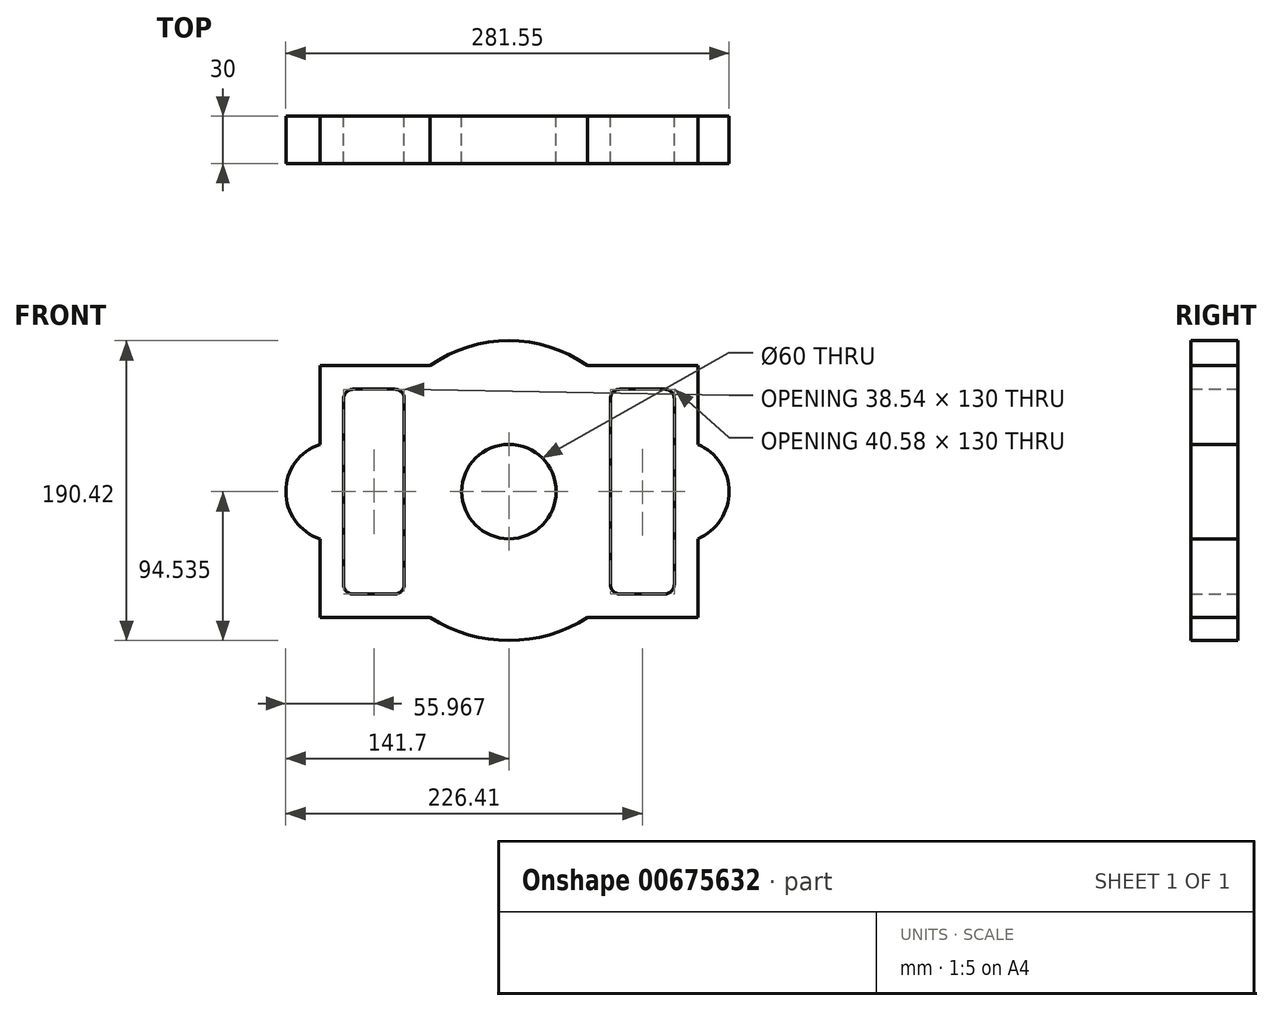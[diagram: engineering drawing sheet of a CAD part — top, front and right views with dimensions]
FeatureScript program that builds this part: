
annotation { "Feature Type Name" : "Feature", "Feature Type Description" : "" }
export const myFeature = defineFeature(function(context is Context, id is Id, definition is map)
    precondition{}
    {
        {
            var Q0;
            Q0=qCreatedBy(makeId("Front.planeOp"),FACE);
            var sketch = newSketch(context, id + "F0", { "sketchPlane" : qUnion([Q0])});
            skLineSegment(sketch, "E0", {"start": v(-20.58, 48.03) * mm, "end": v(-90.58, 48.03) * mm});
            skLineSegment(sketch, "E1", {"start": v(-90.58, 48.03) * mm, "end": v(-90.58, -1.97) * mm});
            skLineSegment(sketch, "E2", {"start": v(-90.58, -111.97) * mm, "end": v(-20.58, -111.97) * mm});
            skLineSegment(sketch, "E3", {"start": v(79.42, 48.03) * mm, "end": v(149.42, 48.03) * mm});
            skLineSegment(sketch, "E4", {"start": v(149.42, 48.03) * mm, "end": v(149.42, -1.97) * mm});
            skLineSegment(sketch, "E5", {"start": v(149.42, -111.97) * mm, "end": v(79.42, -111.97) * mm});
            skArc(sketch, "E6", {"start": v(79.42, 48.03) * mm, "mid": v(29.42, 63.92) * mm, "end": v(-20.58, 48.03) * mm});
            skArc(sketch, "E7", {"start": v(-20.58, -111.97) * mm, "mid": v(29.42, -126.5) * mm, "end": v(79.42, -111.97) * mm});
            skLineSegment(sketch, "E8.trimOffspring", {"start": v(149.42, -61.97) * mm, "end": v(149.42, -111.97) * mm});
            skLineSegment(sketch, "E9.trimOffspring", {"start": v(-90.58, -61.97) * mm, "end": v(-90.58, -111.97) * mm});
            skPoint(sketch, "E10.center.orphan", {"position": v(29.42, 0) * mm});
            skArc(sketch, "E11", {"start": v(-90.58, -1.97) * mm, "mid": v(-112.28, -31.97) * mm, "end": v(-90.58, -61.97) * mm});
            skArc(sketch, "E12", {"start": v(149.42, -61.97) * mm, "mid": v(169.27, -31.97) * mm, "end": v(149.42, -1.97) * mm});
            skCircle(sketch, "E13", {"center": v(29.42, -31.97) * mm, "radius": 30 * mm});
            skLineSegment(sketch, "E14.bottom", {"start": v(99.84, 33.03) * mm, "end": v(128.42, 33.03) * mm});
            skLineSegment(sketch, "E14.top", {"start": v(99.84, -96.97) * mm, "end": v(128.42, -96.97) * mm});
            skLineSegment(sketch, "E14.left", {"start": v(93.84, 27.03) * mm, "end": v(93.84, -90.97) * mm});
            skLineSegment(sketch, "E14.right", {"start": v(134.42, 27.03) * mm, "end": v(134.42, -90.97) * mm});
            skLineSegment(sketch, "E15.bottom", {"start": v(-69.58, 33.03) * mm, "end": v(-43.05, 33.03) * mm});
            skLineSegment(sketch, "E15.top", {"start": v(-69.58, -96.97) * mm, "end": v(-43.05, -96.97) * mm});
            skLineSegment(sketch, "E15.left", {"start": v(-75.58, 27.03) * mm, "end": v(-75.58, -90.97) * mm});
            skLineSegment(sketch, "E15.right", {"start": v(-37.05, 27.03) * mm, "end": v(-37.05, -90.97) * mm});
            skPoint(sketch, "E16.visualSharp", {"position": v(93.84, 33.03) * mm});
            skArc(sketch, "E16.filletArc", {"start": v(99.84, 33.03) * mm, "mid": v(95.6, 31.28) * mm, "end": v(93.84, 27.03) * mm});
            skPoint(sketch, "E17.visualSharp", {"position": v(134.42, 33.03) * mm});
            skArc(sketch, "E17.filletArc", {"start": v(134.42, 27.03) * mm, "mid": v(132.66, 31.28) * mm, "end": v(128.42, 33.03) * mm});
            skPoint(sketch, "E18.visualSharp", {"position": v(134.42, -96.97) * mm});
            skArc(sketch, "E18.filletArc", {"start": v(128.42, -96.97) * mm, "mid": v(132.66, -95.2) * mm, "end": v(134.42, -90.97) * mm});
            skPoint(sketch, "E19.visualSharp", {"position": v(93.84, -96.97) * mm});
            skArc(sketch, "E19.filletArc", {"start": v(93.84, -90.97) * mm, "mid": v(95.6, -95.2) * mm, "end": v(99.84, -96.97) * mm});
            skPoint(sketch, "E20.visualSharp", {"position": v(-37.05, 33.03) * mm});
            skArc(sketch, "E20.filletArc", {"start": v(-37.05, 27.03) * mm, "mid": v(-38.8, 31.28) * mm, "end": v(-43.05, 33.03) * mm});
            skPoint(sketch, "E21.visualSharp", {"position": v(-75.58, 33.03) * mm});
            skArc(sketch, "E21.filletArc", {"start": v(-69.58, 33.03) * mm, "mid": v(-73.82, 31.28) * mm, "end": v(-75.58, 27.03) * mm});
            skPoint(sketch, "E22.visualSharp", {"position": v(-75.58, -96.97) * mm});
            skArc(sketch, "E22.filletArc", {"start": v(-75.58, -90.97) * mm, "mid": v(-73.82, -95.2) * mm, "end": v(-69.58, -96.97) * mm});
            skPoint(sketch, "E23.visualSharp", {"position": v(-37.05, -96.97) * mm});
            skArc(sketch, "E23.filletArc", {"start": v(-43.05, -96.97) * mm, "mid": v(-38.8, -95.2) * mm, "end": v(-37.05, -90.97) * mm});
            skSolve(sketch);
        }
        {
            var Q0;
            Q0 = qSketchRegion(id + "F0", true);
            extrude(context, id + "F1", {"entities" : qUnion([Q0]), "depth" : 30 * mm, "offsetDistance" : 25 * mm});
        }
    });
